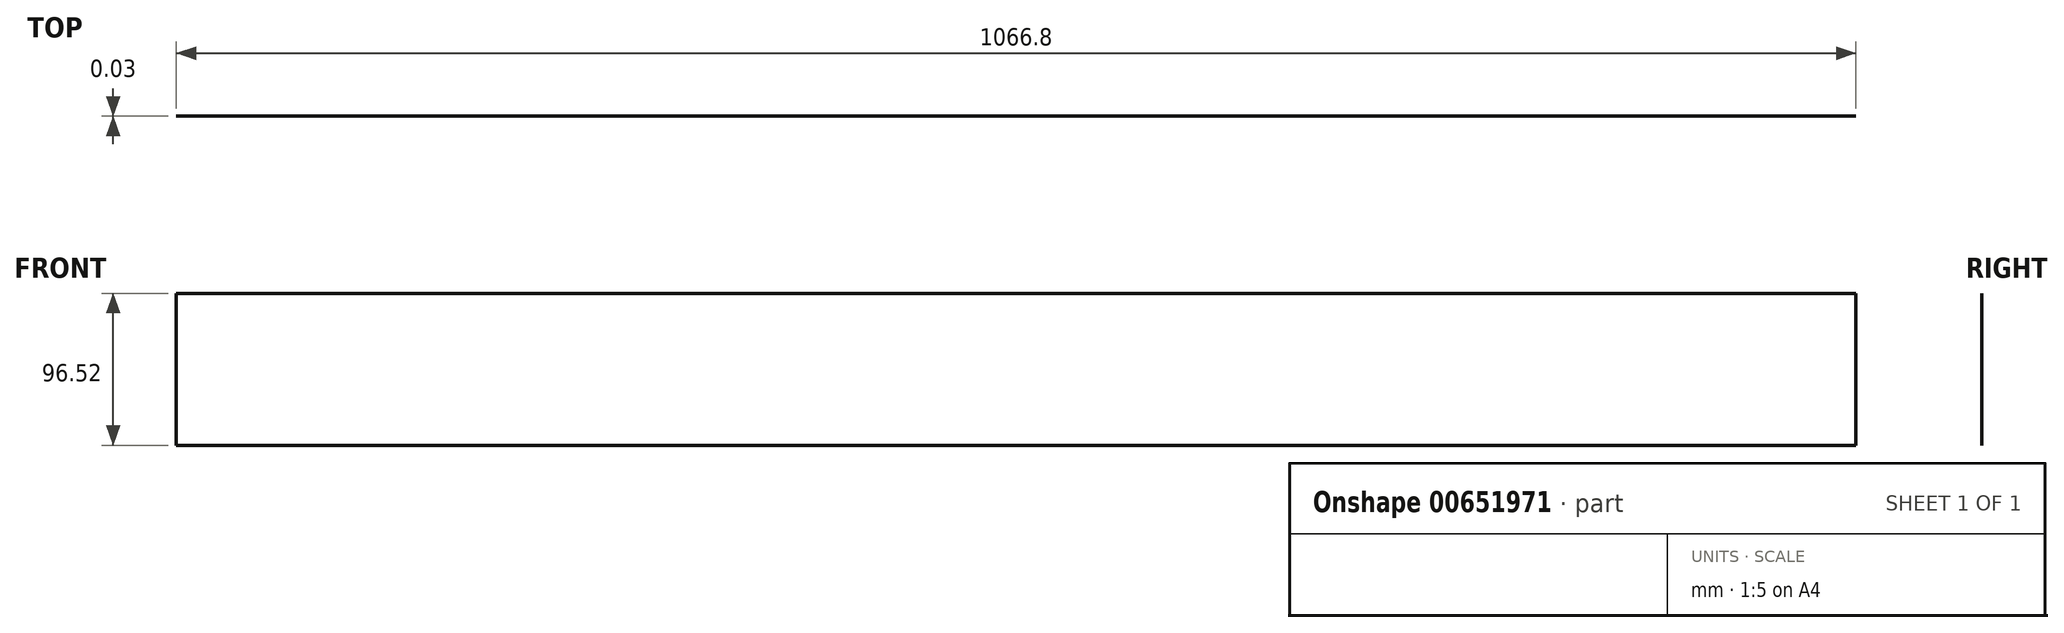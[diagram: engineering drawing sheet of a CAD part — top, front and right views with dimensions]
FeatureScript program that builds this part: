
annotation { "Feature Type Name" : "Feature", "Feature Type Description" : "" }
export const myFeature = defineFeature(function(context is Context, id is Id, definition is map)
    precondition{}
    {
        {
            var Q0;
            Q0=qCreatedBy(makeId("Front.planeOp"),FACE);
            var sketch = newSketch(context, id + "F0", { "sketchPlane" : qUnion([Q0])});
            skLineSegment(sketch, "E0.bottom", {"start": v(-552.45, 0) * mm, "end": v(552.45, 0) * mm});
            skLineSegment(sketch, "E0.top", {"start": v(-552.45, -96.52) * mm, "end": v(552.45, -96.52) * mm});
            skLineSegment(sketch, "E0.left", {"start": v(-552.45, 0) * mm, "end": v(-552.45, -96.52) * mm});
            skLineSegment(sketch, "E0.right", {"start": v(552.45, 0) * mm, "end": v(552.45, -96.52) * mm});
            skSolve(sketch);
        }
        {
            var Q0;
            Q0 = qSketchRegion(id + "F0", true);
            extrude(context, id + "F1", {"entities" : qUnion([Q0]), "depth" : 3 / 101.6 * mm, "offsetDistance" : 25.4 * mm});
        }
        {
            var Q0;
            Q0=makeQuery(id+"F1.opExtrude","SWEPT_FACE",FACE,{"disambiguationData":[OSD([sQuery(id+"F0.wireOp",EDGE,"E0.left")])]});
            var sketch = newSketch(context, id + "F2", { "sketchPlane" : qUnion([Q0])});
            skLineSegment(sketch, "E1.bottom", {"start": v(0, 0) * mm, "end": v(19.05, 0) * mm});
            skLineSegment(sketch, "E1.top", {"start": v(0, -25.4) * mm, "end": v(19.05, -25.4) * mm});
            skLineSegment(sketch, "E1.left", {"start": v(0, 0) * mm, "end": v(0, -25.4) * mm});
            skLineSegment(sketch, "E1.right", {"start": v(19.05, 0) * mm, "end": v(19.05, -25.4) * mm});
            skSolve(sketch);
        }
        {
            var Q0;
            Q0 = qSketchRegion(id + "F2", true);
            extrude(context, id + "F3", {"entities" : qUnion([Q0]), "operationType" : NewBodyOperationType.REMOVE, "oppositeDirection" : true, "depth" : 19.05 * mm, "offsetDistance" : 25.4 * mm});
        }
        {
            var Q0;
            Q0=makeQuery(id+"F1.opExtrude","SWEPT_FACE",FACE,{"disambiguationData":[OSD([sQuery(id+"F0.wireOp",EDGE,"E0.left")])]});
            var sketch = newSketch(context, id + "F4", { "sketchPlane" : qUnion([Q0])});
            skLineSegment(sketch, "E2.bottom", {"start": v(0, -71.12) * mm, "end": v(19.05, -71.12) * mm});
            skLineSegment(sketch, "E2.top", {"start": v(0, -96.52) * mm, "end": v(19.05, -96.52) * mm});
            skLineSegment(sketch, "E2.left", {"start": v(0, -71.12) * mm, "end": v(0, -96.52) * mm});
            skLineSegment(sketch, "E2.right", {"start": v(19.05, -71.12) * mm, "end": v(19.05, -96.52) * mm});
            skSolve(sketch);
        }
        {
            var Q0;
            Q0 = qSketchRegion(id + "F4", true);
            extrude(context, id + "F5", {"entities" : qUnion([Q0]), "operationType" : NewBodyOperationType.REMOVE, "oppositeDirection" : true, "depth" : 19.05 * mm, "offsetDistance" : 25.4 * mm});
        }
        {
            var Q0;
            {var subQ0=sQuery(id+"F4.wireOp",EDGE,"E2.bottom");Q0=makeQuery(id+"F4.imprint","IMPRINT",FACE,{"disambiguationData":[TD([[makeQuery(id+"F4.imprint","IMPRINT",EDGE,{"derivedFrom":subQ0}),1.0]])]});}
            var sketch = newSketch(context, id + "F6", { "sketchPlane" : qUnion([Q0])});
            skLineSegment(sketch, "E3.bottom", {"start": v(0, -25.4) * mm, "end": v(3.17, -25.4) * mm});
            skLineSegment(sketch, "E3.top", {"start": v(0, -71.12) * mm, "end": v(3.17, -71.12) * mm});
            skLineSegment(sketch, "E3.left", {"start": v(0, -25.4) * mm, "end": v(0, -71.12) * mm});
            skLineSegment(sketch, "E3.right", {"start": v(3.17, -25.4) * mm, "end": v(3.17, -71.12) * mm});
            skSolve(sketch);
        }
        {
            var Q0;
            Q0 = qSketchRegion(id + "F6", true);
            extrude(context, id + "F7", {"entities" : qUnion([Q0]), "operationType" : NewBodyOperationType.REMOVE, "oppositeDirection" : true, "depth" : 19.05 * mm, "offsetDistance" : 25.4 * mm});
        }
        {
            var Q0;
            Q0=makeQuery(id+"F1.opExtrude","SWEPT_FACE",FACE,{"disambiguationData":[OSD([sQuery(id+"F0.wireOp",EDGE,"E0.right")])]});
            var sketch = newSketch(context, id + "F8", { "sketchPlane" : qUnion([Q0])});
            skLineSegment(sketch, "E4.bottom", {"start": v(-19.05, 0) * mm, "end": v(0, 0) * mm});
            skLineSegment(sketch, "E4.top", {"start": v(-19.05, -25.4) * mm, "end": v(0, -25.4) * mm});
            skLineSegment(sketch, "E4.left", {"start": v(-19.05, 0) * mm, "end": v(-19.05, -25.4) * mm});
            skLineSegment(sketch, "E4.right", {"start": v(0, 0) * mm, "end": v(0, -25.4) * mm});
            skSolve(sketch);
        }
        {
            var Q0;
            Q0=makeQuery(id+"F8.imprint","IMPRINT",FACE,{"disambiguationData":[TD([[makeQuery(id+"F8.imprint","IMPRINT",EDGE,{"derivedFrom":sQuery(id+"F8.wireOp",EDGE,"E4.bottom")}),-1.0]])]});
            extrude(context, id + "F9", {"entities" : qUnion([Q0]), "operationType" : NewBodyOperationType.REMOVE, "oppositeDirection" : true, "depth" : 19.05 * mm, "offsetDistance" : 25.4 * mm});
        }
        {
            var Q0;
            Q0=makeQuery(id+"F1.opExtrude","SWEPT_FACE",FACE,{"disambiguationData":[OSD([sQuery(id+"F0.wireOp",EDGE,"E0.right")])]});
            var sketch = newSketch(context, id + "F10", { "sketchPlane" : qUnion([Q0])});
            skLineSegment(sketch, "E5.bottom", {"start": v(0, -96.52) * mm, "end": v(-19.05, -96.52) * mm});
            skLineSegment(sketch, "E5.top", {"start": v(0, -71.12) * mm, "end": v(-19.05, -71.12) * mm});
            skLineSegment(sketch, "E5.left", {"start": v(0, -96.52) * mm, "end": v(0, -71.12) * mm});
            skLineSegment(sketch, "E5.right", {"start": v(-19.05, -96.52) * mm, "end": v(-19.05, -71.12) * mm});
            skSolve(sketch);
        }
        {
            var Q0;
            Q0=makeQuery(id+"F10.imprint","IMPRINT",FACE,{"disambiguationData":[TD([[makeQuery(id+"F10.imprint","IMPRINT",EDGE,{"derivedFrom":sQuery(id+"F10.wireOp",EDGE,"E5.bottom")}),1.0]])]});
            extrude(context, id + "F11", {"entities" : qUnion([Q0]), "operationType" : NewBodyOperationType.REMOVE, "oppositeDirection" : true, "depth" : 19.05 * mm, "offsetDistance" : 25.4 * mm});
        }
        {
            var Q0;
            Q0=makeQuery(id+"F1.opExtrude","SWEPT_FACE",FACE,{"disambiguationData":[OSD([sQuery(id+"F0.wireOp",EDGE,"E0.right")])]});
            var sketch = newSketch(context, id + "F12", { "sketchPlane" : qUnion([Q0])});
            skLineSegment(sketch, "E6.bottom", {"start": v(-19.05, -25.4) * mm, "end": v(-15.87, -25.4) * mm});
            skLineSegment(sketch, "E6.top", {"start": v(-19.05, -71.12) * mm, "end": v(-15.87, -71.12) * mm});
            skLineSegment(sketch, "E6.left", {"start": v(-19.05, -25.4) * mm, "end": v(-19.05, -71.12) * mm});
            skLineSegment(sketch, "E6.right", {"start": v(-15.87, -25.4) * mm, "end": v(-15.87, -71.12) * mm});
            skSolve(sketch);
        }
        {
            var Q0;
            Q0=makeQuery(id+"F12.imprint","IMPRINT",FACE,{"disambiguationData":[TD([[makeQuery(id+"F12.imprint","IMPRINT",EDGE,{"derivedFrom":sQuery(id+"F12.wireOp",EDGE,"E6.bottom")}),-1.0]])]});
            extrude(context, id + "F13", {"entities" : qUnion([Q0]), "operationType" : NewBodyOperationType.REMOVE, "oppositeDirection" : true, "depth" : 19.05 * mm, "offsetDistance" : 25.4 * mm});
        }
        {
            var Q0;
            Q0=makeQuery(id+"F1.opExtrude","SWEPT_FACE",FACE,{"disambiguationData":[OSD([sQuery(id+"F0.wireOp",EDGE,"E0.right")])]});
            var sketch = newSketch(context, id + "F14", { "sketchPlane" : qUnion([Q0])});
            skLineSegment(sketch, "E7.bottom", {"start": v(0, -25.4) * mm, "end": v(-3.18, -25.4) * mm});
            skLineSegment(sketch, "E7.top", {"start": v(0, -71.12) * mm, "end": v(-3.17, -71.12) * mm});
            skLineSegment(sketch, "E7.left", {"start": v(0, -25.4) * mm, "end": v(0, -71.12) * mm});
            skLineSegment(sketch, "E7.right", {"start": v(-3.18, -25.4) * mm, "end": v(-3.17, -71.12) * mm});
            skSolve(sketch);
        }
        {
            var Q0;
            Q0 = qSketchRegion(id + "F14", true);
            extrude(context, id + "F15", {"entities" : qUnion([Q0]), "operationType" : NewBodyOperationType.REMOVE, "oppositeDirection" : true, "depth" : 19.05 * mm, "offsetDistance" : 25.4 * mm});
        }
    });
